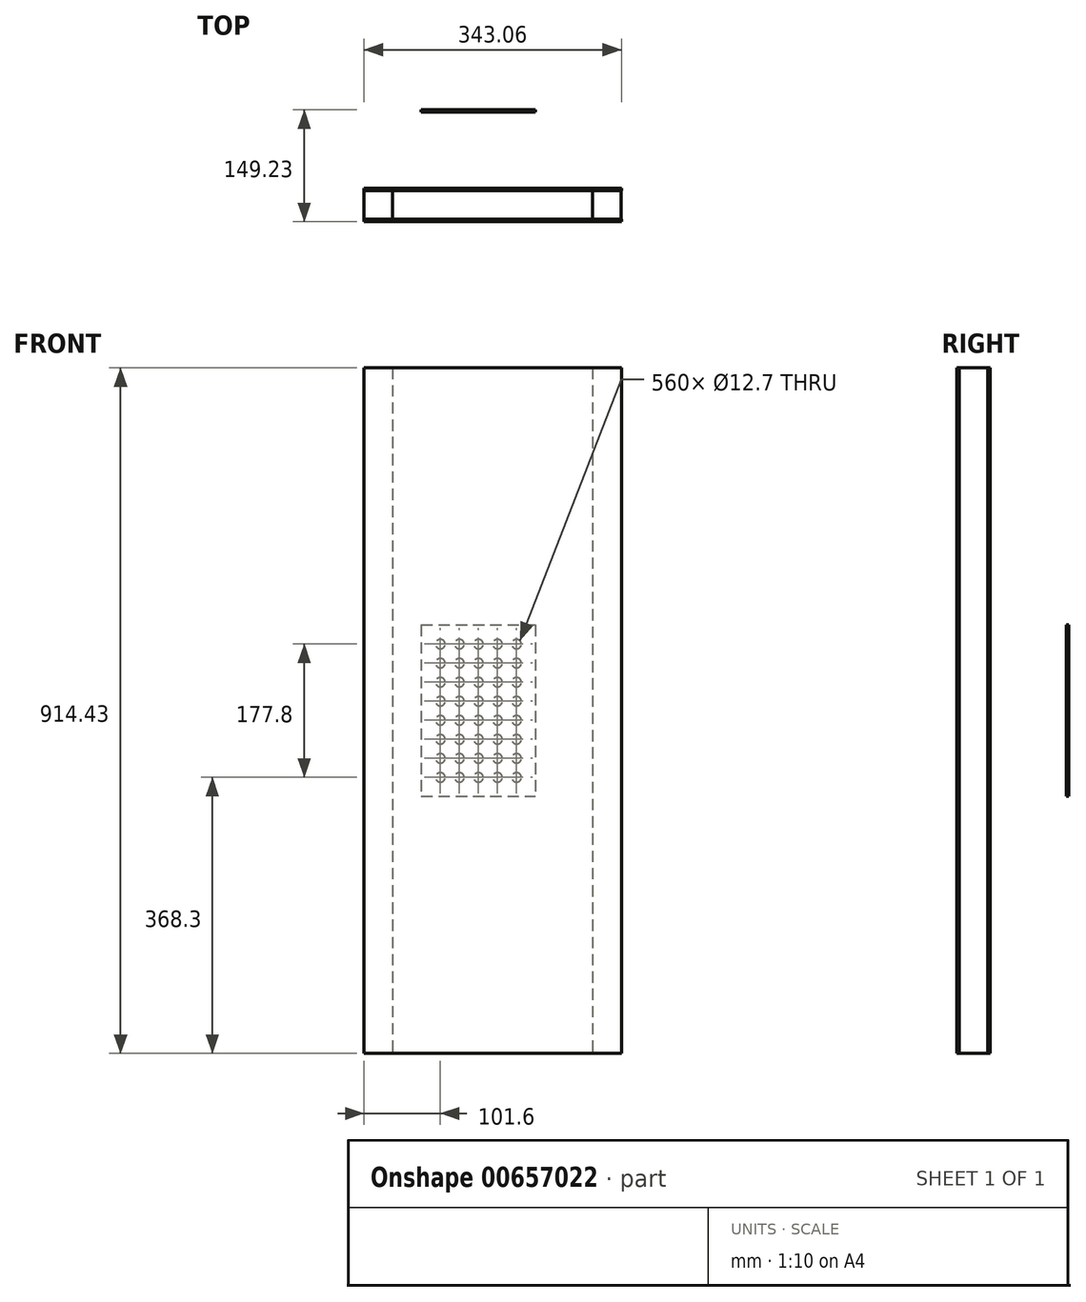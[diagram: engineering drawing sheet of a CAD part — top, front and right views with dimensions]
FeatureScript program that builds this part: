
annotation { "Feature Type Name" : "Feature", "Feature Type Description" : "" }
export const myFeature = defineFeature(function(context is Context, id is Id, definition is map)
    precondition{}
    {
        {
            var Q0;
            Q0=qCreatedBy(makeId("Front.planeOp"),FACE);
            var sketch = newSketch(context, id + "F0", { "sketchPlane" : qUnion([Q0])});
            skLineSegment(sketch, "E0.bottom", {"start": v(-76.2, 114.3) * mm, "end": v(76.2, 114.3) * mm});
            skLineSegment(sketch, "E0.top", {"start": v(-76.2, -114.3) * mm, "end": v(76.2, -114.3) * mm});
            skLineSegment(sketch, "E0.left", {"start": v(-76.2, 114.3) * mm, "end": v(-76.2, -114.3) * mm});
            skLineSegment(sketch, "E0.right", {"start": v(76.2, 114.3) * mm, "end": v(76.2, -114.3) * mm});
            skPoint(sketch, "E0.middle", {"position": v(0, 0) * mm});
            skCircle(sketch, "E1", {"center": v(-50.8, -12.7) * mm, "radius": 6.35 * mm});
            skCircle(sketch, "E2", {"center": v(-25.4, 12.7) * mm, "radius": 6.35 * mm});
            skCircle(sketch, "E3", {"center": v(50.8, -12.7) * mm, "radius": 6.35 * mm});
            skCircle(sketch, "E4", {"center": v(25.4, 12.7) * mm, "radius": 6.35 * mm});
            skCircle(sketch, "E5", {"center": v(0, -12.7) * mm, "radius": 6.35 * mm});
            skCircle(sketch, "E6", {"center": v(-50.8, 38.1) * mm, "radius": 6.35 * mm});
            skCircle(sketch, "E7", {"center": v(-50.8, 63.5) * mm, "radius": 6.35 * mm});
            skCircle(sketch, "E8", {"center": v(-50.8, 88.9) * mm, "radius": 6.35 * mm});
            skCircle(sketch, "E9", {"center": v(-25.4, 38.1) * mm, "radius": 6.35 * mm});
            skCircle(sketch, "E10", {"center": v(0, 88.9) * mm, "radius": 6.35 * mm});
            skCircle(sketch, "E11", {"center": v(25.4, 38.1) * mm, "radius": 6.35 * mm});
            skCircle(sketch, "E12", {"center": v(50.8, 63.5) * mm, "radius": 6.35 * mm});
            skCircle(sketch, "E13", {"center": v(-25.4, 88.9) * mm, "radius": 6.35 * mm});
            skCircle(sketch, "E14", {"center": v(0, 38.1) * mm, "radius": 6.35 * mm});
            skCircle(sketch, "E15", {"center": v(25.4, 88.9) * mm, "radius": 6.35 * mm});
            skCircle(sketch, "E16", {"center": v(50.8, 38.1) * mm, "radius": 6.35 * mm});
            skCircle(sketch, "E17", {"center": v(-25.4, 63.5) * mm, "radius": 6.35 * mm});
            skCircle(sketch, "E18", {"center": v(0, 63.5) * mm, "radius": 6.35 * mm});
            skCircle(sketch, "E19", {"center": v(25.4, 63.5) * mm, "radius": 6.35 * mm});
            skCircle(sketch, "E20", {"center": v(50.8, 88.9) * mm, "radius": 6.35 * mm});
            skCircle(sketch, "E21", {"center": v(-50.8, 12.7) * mm, "radius": 6.35 * mm});
            skCircle(sketch, "E22", {"center": v(-25.4, -88.9) * mm, "radius": 6.35 * mm});
            skCircle(sketch, "E23", {"center": v(0, 12.7) * mm, "radius": 6.35 * mm});
            skCircle(sketch, "E24", {"center": v(25.4, -12.7) * mm, "radius": 6.35 * mm});
            skCircle(sketch, "E25", {"center": v(50.8, 12.7) * mm, "radius": 6.35 * mm});
            skCircle(sketch, "E26", {"center": v(-50.8, -38.1) * mm, "radius": 6.35 * mm});
            skCircle(sketch, "E27", {"center": v(-25.4, -12.7) * mm, "radius": 6.35 * mm});
            skCircle(sketch, "E28", {"center": v(0, -88.9) * mm, "radius": 6.35 * mm});
            skCircle(sketch, "E29", {"center": v(25.4, -38.1) * mm, "radius": 6.35 * mm});
            skCircle(sketch, "E30", {"center": v(50.8, -38.1) * mm, "radius": 6.35 * mm});
            skCircle(sketch, "E31", {"center": v(-50.8, -88.9) * mm, "radius": 6.35 * mm});
            skCircle(sketch, "E32", {"center": v(-25.4, -38.1) * mm, "radius": 6.35 * mm});
            skCircle(sketch, "E33", {"center": v(0, -38.1) * mm, "radius": 6.35 * mm});
            skCircle(sketch, "E34", {"center": v(25.4, -88.9) * mm, "radius": 6.35 * mm});
            skCircle(sketch, "E35", {"center": v(50.8, -88.9) * mm, "radius": 6.35 * mm});
            skCircle(sketch, "E36", {"center": v(-50.8, -63.5) * mm, "radius": 6.35 * mm});
            skCircle(sketch, "E37", {"center": v(-25.4, -63.5) * mm, "radius": 6.35 * mm});
            skCircle(sketch, "E38", {"center": v(0, -63.5) * mm, "radius": 6.35 * mm});
            skCircle(sketch, "E39", {"center": v(25.4, -63.5) * mm, "radius": 6.35 * mm});
            skCircle(sketch, "E40", {"center": v(50.8, -63.5) * mm, "radius": 6.35 * mm});
            skSolve(sketch);
        }
        {
            var Q0;
            Q0=makeQuery(id+"F0.imprint","IMPRINT",FACE,{"disambiguationData":[TD([[makeQuery(id+"F0.imprint","IMPRINT",EDGE,{"derivedFrom":sQuery(id+"F0.wireOp",EDGE,"E0.bottom")}),-1.0]])]});
            extrude(context, id + "F1", {"entities" : qUnion([Q0]), "depth" : 3.17 * mm, "offsetDistance" : 25.4 * mm});
        }
        {
            var Q0;
            Q0=qCreatedBy(makeId("Right.planeOp"),FACE);
            var sketch = newSketch(context, id + "F2", { "sketchPlane" : qUnion([Q0])});
            skLineSegment(sketch, "E41.bottom", {"start": v(-107.95, 457.2) * mm, "end": v(-146.05, 457.2) * mm});
            skLineSegment(sketch, "E41.top", {"start": v(-107.95, -457.2) * mm, "end": v(-146.05, -457.2) * mm});
            skLineSegment(sketch, "E41.left", {"start": v(-107.95, 457.2) * mm, "end": v(-107.95, -457.2) * mm});
            skLineSegment(sketch, "E41.right", {"start": v(-146.05, 457.2) * mm, "end": v(-146.05, -457.2) * mm});
            skPoint(sketch, "E41.middle", {"position": v(-127, 0) * mm});
            skSolve(sketch);
        }
        {
            var Q0;
            Q0=makeQuery(id+"F2.imprint","IMPRINT",FACE,{"disambiguationData":[TD([[makeQuery(id+"F2.imprint","IMPRINT",EDGE,{"derivedFrom":sQuery(id+"F2.wireOp",EDGE,"E41.bottom")}),1.0]])]});
            extrude(context, id + "F3", {"entities" : qUnion([Q0]), "depth" : 38.1 * mm, "offsetDistance" : 25.4 * mm});
        }
        {
            var Q0;
            Q0=makeQuery(id+"F3.opExtrude","SWEPT_BODY",BODY,{"disambiguationData":[OSD([sQuery(id+"F2.wireOp",EDGE,"E41.bottom"),sQuery(id+"F2.wireOp",EDGE,"E41.top"),sQuery(id+"F2.wireOp",EDGE,"E41.left"),sQuery(id+"F2.wireOp",EDGE,"E41.right")])]});
            var Q1;
            Q1=qCreatedBy(makeId("Right.planeOp"),FACE);
            transform(context, id + "F4", {"entities" : qUnion([Q0]), "transformType" : TransformType.TRANSLATION_DISTANCE, "transformDirection" : qUnion([Q1]), "distance" : 304.8 * mm, "makeCopy" : true});
        }
        {
            var Q0;
            Q0=makeQuery(id+"F4.opPattern","COPY",BODY,{"derivedFrom":makeQuery(id+"F3.opExtrude","SWEPT_BODY",BODY,{"disambiguationData":[OSD([sQuery(id+"F2.wireOp",EDGE,"E41.bottom"),sQuery(id+"F2.wireOp",EDGE,"E41.top"),sQuery(id+"F2.wireOp",EDGE,"E41.left"),sQuery(id+"F2.wireOp",EDGE,"E41.right")])]}),"instanceName":"1"});
            var Q1;
            Q1=makeQuery(id+"F3.opExtrude","SWEPT_BODY",BODY,{"disambiguationData":[OSD([sQuery(id+"F2.wireOp",EDGE,"E41.bottom"),sQuery(id+"F2.wireOp",EDGE,"E41.top"),sQuery(id+"F2.wireOp",EDGE,"E41.left"),sQuery(id+"F2.wireOp",EDGE,"E41.right")])]});
            var Q2;
            Q2=qCreatedBy(makeId("Right.planeOp"),FACE);
            transform(context, id + "F5", {"entities" : qUnion([Q0, Q1]), "transformType" : TransformType.TRANSLATION_DISTANCE, "transformDirection" : qUnion([Q2]), "distance" : 152.4 * mm, "oppositeDirection" : true, "makeCopy" : false});
        }
        {
            var Q0;
            Q0=makeQuery(id+"F3.opExtrude","SWEPT_FACE",FACE,{"disambiguationData":[OSD([sQuery(id+"F2.wireOp",EDGE,"E41.right")])]});
            var sketch = newSketch(context, id + "F6", { "sketchPlane" : qUnion([Q0])});
            skLineSegment(sketch, "E42.bottom", {"start": v(-152.4, -457.2) * mm, "end": v(190.66, -457.2) * mm});
            skLineSegment(sketch, "E42.top", {"start": v(-152.4, 457.23) * mm, "end": v(190.66, 457.23) * mm});
            skLineSegment(sketch, "E42.left", {"start": v(-152.4, -457.2) * mm, "end": v(-152.4, 457.23) * mm});
            skLineSegment(sketch, "E42.right", {"start": v(190.66, -457.2) * mm, "end": v(190.66, 457.23) * mm});
            skSolve(sketch);
        }
        {
            var Q0;
            {var subQ3=sQuery(id+"F6.wireOp",EDGE,"E42.top");Q0=makeQuery(id+"F6.imprint","IMPRINT",FACE,{"disambiguationData":[TD([[makeQuery(id+"F6.imprint","IMPRINT",EDGE,{"derivedFrom":subQ3}),-1.0]])]});}
            var Q1;
            {var subQ3=sQuery(id+"F2.wireOp",EDGE,"E41.right");var subQ4=makeQuery(id+"F3.opExtrude","CAP_EDGE",EDGE,{"disambiguationData":[OSD([subQ3])],"isStart":false});Q1=makeQuery(id+"F6.imprint","IMPRINT",FACE,{"disambiguationData":[TD([[makeQuery(id+"F6.imprint","IMPRINT",EDGE,{"derivedFrom":subQ4}),-1.0]])]});}
            extrude(context, id + "F7", {"entities" : qUnion([Q0, Q1]), "depth" : 3.17 * mm, "offsetDistance" : 25.4 * mm});
        }
        {
            var Q0;
            Q0=makeQuery(id+"F7.opExtrude","SWEPT_BODY",BODY,{"disambiguationData":[OSD([sQuery(id+"F6.wireOp",EDGE,"E42.bottom"),sQuery(id+"F6.wireOp",EDGE,"E42.top"),sQuery(id+"F6.wireOp",EDGE,"E42.left"),sQuery(id+"F6.wireOp",EDGE,"E42.right")])]});
            var Q1;
            Q1=makeQuery(id+"F7.opExtrude","CAP_FACE",FACE,{"disambiguationData":[OSD([sQuery(id+"F6.wireOp",EDGE,"E42.bottom"),sQuery(id+"F6.wireOp",EDGE,"E42.top"),sQuery(id+"F6.wireOp",EDGE,"E42.left"),sQuery(id+"F6.wireOp",EDGE,"E42.right")])],"isStart":false});
            transform(context, id + "F8", {"entities" : qUnion([Q0]), "transformType" : TransformType.TRANSLATION_DISTANCE, "transformDirection" : qUnion([Q1]), "distance" : 41.27 * mm, "oppositeDirection" : true, "makeCopy" : true});
        }
    });
